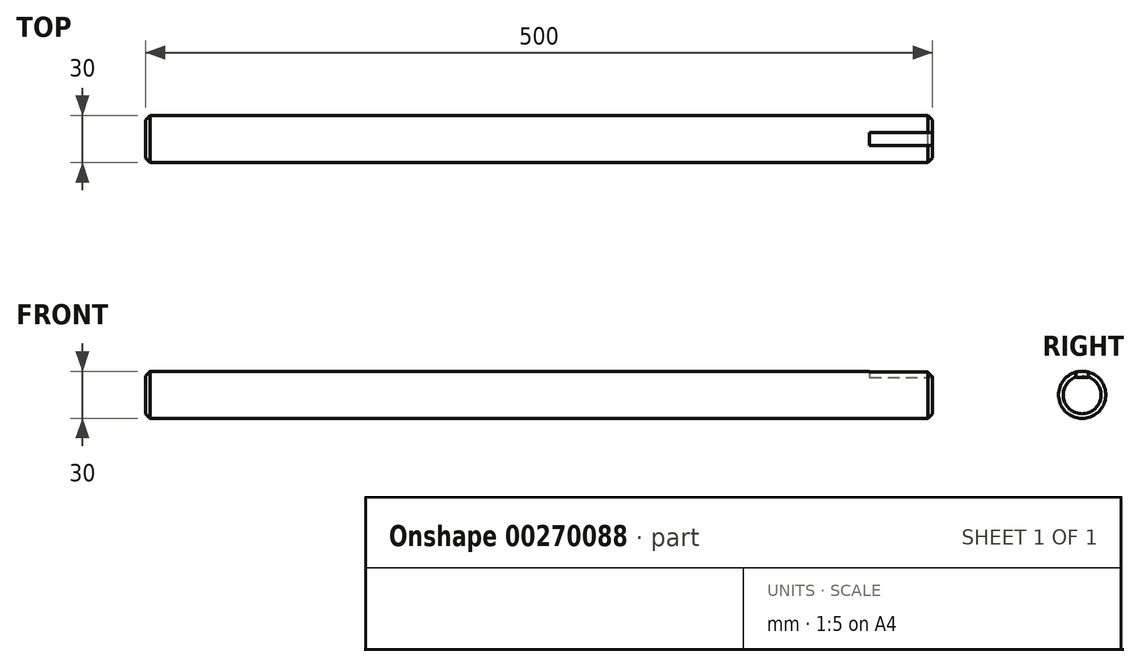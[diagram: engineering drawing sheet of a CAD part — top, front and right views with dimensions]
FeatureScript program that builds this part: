
annotation { "Feature Type Name" : "Feature", "Feature Type Description" : "" }
export const myFeature = defineFeature(function(context is Context, id is Id, definition is map)
    precondition{}
    {
        {
            var Q0;
            Q0=qCreatedBy(makeId("Top.planeOp"),FACE);
            var sketch = newSketch(context, id + "F0", { "sketchPlane" : qUnion([Q0])});
            skLineSegment(sketch, "E0.bottom", {"start": v(-250, 15) * mm, "end": v(250, 15) * mm});
            skLineSegment(sketch, "E0.top", {"start": v(-250, 0) * mm, "end": v(250, 0) * mm});
            skLineSegment(sketch, "E0.left", {"start": v(-250, 15) * mm, "end": v(-250, 0) * mm});
            skLineSegment(sketch, "E0.right", {"start": v(250, 15) * mm, "end": v(250, 0) * mm});
            skPoint(sketch, "E1", {"position": v(0, 15) * mm});
            skSolve(sketch);
        }
        {
            var Q0;
            Q0=makeQuery(id+"F0.imprint","IMPRINT",FACE,{"disambiguationData":[TD([[makeQuery(id+"F0.imprint","IMPRINT",EDGE,{"derivedFrom":sQuery(id+"F0.wireOp",EDGE,"E0.bottom")}),-1.0]])]});
            var Q1;
            Q1=sQuery(id+"F0.wireOp",EDGE,"E0.top");
            revolve(context, id + "F1", {"entities" : qUnion([Q0]), "axis" : qUnion([Q1]), "revolveType" : RevolveType.FULL});
        }
        {
            var Q0;
            Q0=makeQuery(id+"F1.opRevolve","SWEPT_FACE",FACE,{"disambiguationData":[OSD([sQuery(id+"F0.wireOp",EDGE,"E0.right")])]});
            var sketch = newSketch(context, id + "F2", { "sketchPlane" : qUnion([Q0])});
            skLineSegment(sketch, "E2", {"start": v(0, 21.91) * mm, "end": v(0, -20.73) * mm, "construction": true});
            skLineSegment(sketch, "E3", {"start": v(-4, 14.46) * mm, "end": v(-4, 11.16) * mm});
            skLineSegment(sketch, "E4", {"start": v(-4, 11.16) * mm, "end": v(4, 11.16) * mm});
            skLineSegment(sketch, "E5", {"start": v(4, 11.16) * mm, "end": v(4, 14.46) * mm});
            skPoint(sketch, "E6", {"position": v(0, 11.16) * mm});
            skSolve(sketch);
        }
        {
            var Q0;
            {var subQ0=sQuery(id+"F2.wireOp",EDGE,"E3");Q0=makeQuery(id+"F2.imprint","IMPRINT",FACE,{"disambiguationData":[TD([[makeQuery(id+"F2.imprint","IMPRINT",EDGE,{"derivedFrom":subQ0}),1.0]])]});}
            extrude(context, id + "F3", {"entities" : qUnion([Q0]), "operationType" : NewBodyOperationType.REMOVE, "oppositeDirection" : true, "depth" : 40 * mm});
        }
        {
            var Q0;
            Q0=makeQuery(id+"F1.opRevolve","SWEPT_EDGE",EDGE,{"disambiguationData":[OSD([sQuery(id+"F0.wireOp",EDGE,"E0.bottom"),sQuery(id+"F0.wireOp",EDGE,"E0.right")])]});
            var Q1;
            Q1=makeQuery(id+"F1.opRevolve","SWEPT_EDGE",EDGE,{"disambiguationData":[OSD([sQuery(id+"F0.wireOp",EDGE,"E0.bottom"),sQuery(id+"F0.wireOp",EDGE,"E0.left")])]});
            chamfer(context, id + "F4", {"entities" : qUnion([Q0, Q1]), "chamferType" : ChamferType.OFFSET_ANGLE, "width" : 3 * mm, "oppositeDirection" : false, "angle" : 45 * degree, "tangentPropagation" : true});
        }
    });
